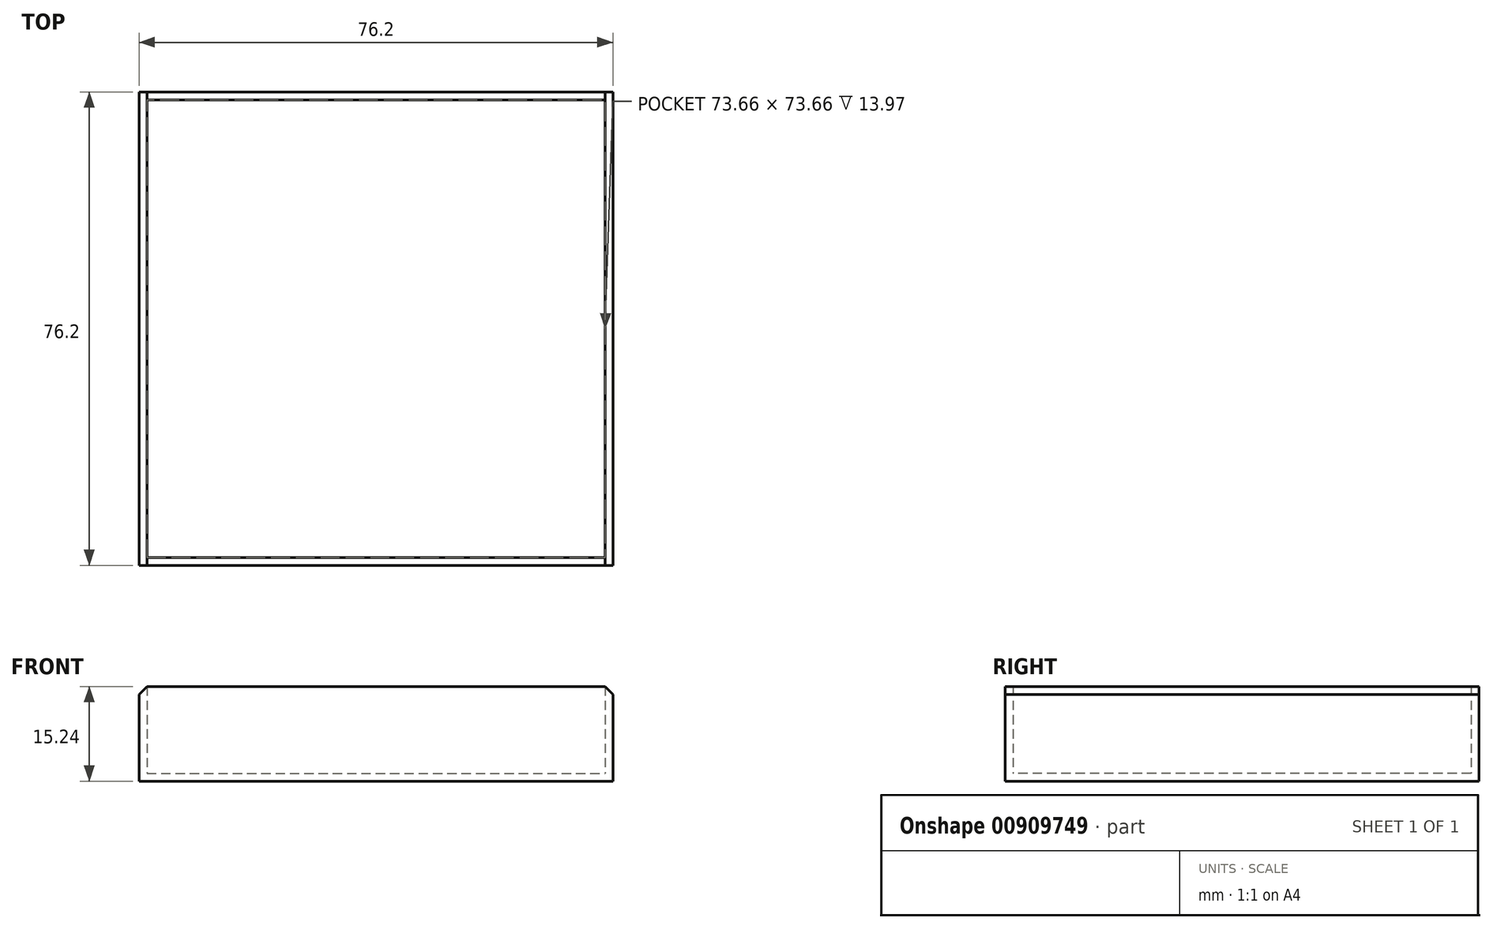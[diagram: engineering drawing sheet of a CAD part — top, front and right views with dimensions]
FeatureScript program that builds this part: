
annotation { "Feature Type Name" : "Feature", "Feature Type Description" : "" }
export const myFeature = defineFeature(function(context is Context, id is Id, definition is map)
    precondition{}
    {
        {
            var Q0;
            Q0=qCreatedBy(makeId("Top.planeOp"),FACE);
            var sketch = newSketch(context, id + "F0", { "sketchPlane" : qUnion([Q0])});
            skLineSegment(sketch, "E0.bottom", {"start": v(-38.1, 38.1) * mm, "end": v(38.1, 38.1) * mm});
            skLineSegment(sketch, "E0.top", {"start": v(-38.1, -38.1) * mm, "end": v(38.1, -38.1) * mm});
            skLineSegment(sketch, "E0.left", {"start": v(-38.1, 38.1) * mm, "end": v(-38.1, -38.1) * mm});
            skLineSegment(sketch, "E0.right", {"start": v(38.1, 38.1) * mm, "end": v(38.1, -38.1) * mm});
            skPoint(sketch, "E0.middle", {"position": v(0, 0) * mm});
            skLineSegment(sketch, "E1.bottom", {"start": v(-36.83, 36.83) * mm, "end": v(36.83, 36.83) * mm});
            skLineSegment(sketch, "E1.top", {"start": v(-36.83, -36.83) * mm, "end": v(36.83, -36.83) * mm});
            skLineSegment(sketch, "E1.left", {"start": v(-36.83, 36.83) * mm, "end": v(-36.83, -36.83) * mm});
            skLineSegment(sketch, "E1.right", {"start": v(36.83, 36.83) * mm, "end": v(36.83, -36.83) * mm});
            skSolve(sketch);
        }
        {
            var Q0;
            Q0=makeQuery(id+"F0.imprint","IMPRINT",FACE,{"disambiguationData":[TD([[makeQuery(id+"F0.imprint","IMPRINT",EDGE,{"derivedFrom":sQuery(id+"F0.wireOp",EDGE,"E0.bottom")}),-1.0]])]});
            extrude(context, id + "F1", {"entities" : qUnion([Q0]), "depth" : 13.97 * mm, "offsetDistance" : 25.4 * mm});
        }
        {
            var Q0;
            Q0=makeQuery(id+"F1.opExtrude","CAP_EDGE",EDGE,{"disambiguationData":[OSD([sQuery(id+"F0.wireOp",EDGE,"E0.left")])],"isStart":false});
            var Q1;
            Q1=makeQuery(id+"F1.opExtrude","CAP_EDGE",EDGE,{"disambiguationData":[OSD([sQuery(id+"F0.wireOp",EDGE,"E0.right")])],"isStart":false});
            chamfer(context, id + "F2", {"entities" : qUnion([Q0, Q1]), "width" : 1.27 * mm, "tangentPropagation" : true});
        }
        {
            var Q0;
            Q0=makeQuery(id+"F1.opExtrude","CAP_FACE",FACE,{"disambiguationData":[OSD([sQuery(id+"F0.wireOp",EDGE,"E0.bottom"),sQuery(id+"F0.wireOp",EDGE,"E0.top"),sQuery(id+"F0.wireOp",EDGE,"E0.left"),sQuery(id+"F0.wireOp",EDGE,"E0.right"),sQuery(id+"F0.wireOp",EDGE,"E1.bottom"),sQuery(id+"F0.wireOp",EDGE,"E1.top"),sQuery(id+"F0.wireOp",EDGE,"E1.left"),sQuery(id+"F0.wireOp",EDGE,"E1.right")])],"isStart":true});
            var sketch = newSketch(context, id + "F3", { "sketchPlane" : qUnion([Q0])});
            skLineSegment(sketch, "E2.bottom", {"start": v(-38.1, 38.1) * mm, "end": v(38.1, 38.1) * mm});
            skLineSegment(sketch, "E2.top", {"start": v(-38.1, -38.1) * mm, "end": v(38.1, -38.1) * mm});
            skLineSegment(sketch, "E2.left", {"start": v(-38.1, 38.1) * mm, "end": v(-38.1, -38.1) * mm});
            skLineSegment(sketch, "E2.right", {"start": v(38.1, 38.1) * mm, "end": v(38.1, -38.1) * mm});
            skPoint(sketch, "E2.middle", {"position": v(0, 0) * mm});
            skSolve(sketch);
        }
        {
            var Q0;
            Q0 = qSketchRegion(id + "F3", true);
            extrude(context, id + "F4", {"entities" : qUnion([Q0]), "operationType" : NewBodyOperationType.ADD, "depth" : 1.27 * mm, "offsetDistance" : 25.4 * mm});
        }
    });
